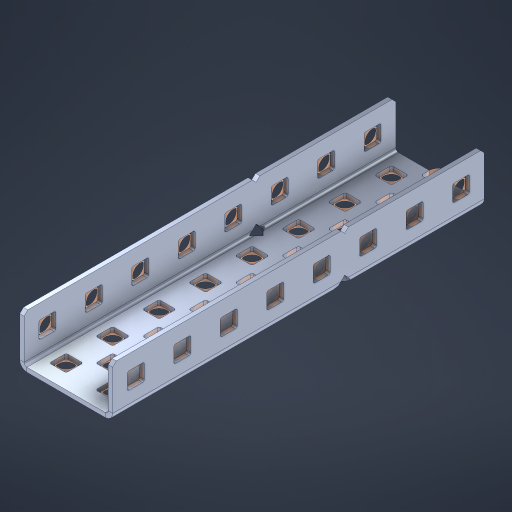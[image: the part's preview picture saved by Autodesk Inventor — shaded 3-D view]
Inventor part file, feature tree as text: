
AUTODESK INVENTOR PART (.ipt)
format: ipt  version: 2023 (Build 270158000, 158)  size: 817,152 bytes
history: native  units: in
note: dims shown in document units (in); Inventor stores cm internally (conversion verified against a paired STEP export)
features: other x47, extrude x38, sheet_metal_op x11, sketch x10, pattern_linear x2, mirror x1, chamfer x1
ambient origin geometry x8: Origin, YZ Plane, XZ Plane, XY Plane, X Axis, Y Axis, Z Axis, Center Point
bodies: Solid1 (feature_tree), Body (feature_tree)
feature tree (110):
  sheet_metal_op  "Flanges"
  other  "Flange Pattern Plane"
  other  "Flange Pattern Sketch"
  sheet_metal_op  "Flange Pattern"
  sheet_metal_op  "Body Pattern"
  pattern_linear  "Center Pattern"  Spacing1=0.0469in  [1 undecoded]
  other  "Arc Length"
  mirror  "Notch Mirror"
  pattern_linear  "Notch Pattern"  Spacing1=0.182in  [1 undecoded]
  chamfer  "End Chamfer"
  extrude  "Half Cut"  Depth=0.02in
  sketch  "Sketch1"  dims[d0=1.0in]
  other  "Plate1"
  sketch  "Sketch2"  dims[d1=4.0in]
  other  "Plate2"
  sheet_metal_op  "Bend1"
  sheet_metal_op  "Corner1"
  sketch  "Sketch3"  dims[d2=0.0469in]
  sketch  "Sketch7"  dims[d3=0.0469in]
  other  "Srf1"
  other  "Srf2"
  sketch  "Sketch8"  dims[d4=0.0234in]
  sketch  "Sketch9"  dims[d5=0.0938in]
  other  "Srf91"
  sheet_metal_op  "Body Pattern Sketch"
  other  "Srf92"
  sketch  "Sketch13"  dims[d6=0.0469in]
  sketch  "Sketch14"  dims[d7=0.5in d8=90.0deg d9=0.0312in]
  sketch  "Sketch15"  dims[d10=0.1875in]
  sketch  "Sketch16"  dims[d11=0.0469in d12=0.0469in d16=0.182in d17=0.02in d18=0.0469in d19=0.0in d20=0.25in d21=0.25in d38=3.1496in d40=0.5in d41=0.7874in d43=1.0in d46=0.172in d47=1.0in d48=0.0in d49=0.182in d50=0.02in d51=0.25in d52=0.25in d53=0.0469in d54=0.0in d55=0.172in d56=1.0in d57=0.0in d58=0.25in d60=3.1496in d62=0.5in d63=0.7874in d65=0.5in d85=0.1227in d86=0.1659in d88=0.04in d89=0.0469in d90=0.0in d91=0.04in d92=0.0491in d95=2.5in d96=0.04in d97=0.25in d98=45.0deg d99=0.25in d100=0.5in d101=0.0in d102=2.497in d106=0.182in d107=0.02in d108=0.5in d109=0.5in d110=0.0469in d111=0.0in d112=0.172in d113=0.5in d114=0.0in d117=0.5in d118=0.5in d119=0.5in]
  other  "Srf786"
  other  "Srf823"
  other  "Srf824"
  other  "Srf825"
  other  "Srf826"
  other  "Srf827"
  other  "Srf828"
  other  "Srf829"
  other  "Srf856"
  other  "Srf857"
  other  "Srf858"
  other  "Srf859"
  other  "Srf860"
  other  "Srf861"
  other  "Srf862"
  other  "Srf889"
  other  "Srf890"
  other  "Srf891"
  other  "Srf892"
  other  "Srf893"
  other  "Srf894"
  other  "Srf895"
  other  "Srf922"
  other  "Srf923"
  other  "Srf924"
  other  "Srf925"
  other  "Srf926"
  other  "Srf959"
  other  "Srf960"
  other  "Srf961"
  other  "Srf962"
  other  "Srf963"
  other  "Srf1143"
  other  "Srf1144"
  other  "Srf1199"
  other  "Srf1200"
  sheet_metal_op  "Flange Stamp"
  sheet_metal_op  "Flange Circle"
  sheet_metal_op  "Body Stamp"
  sheet_metal_op  "Body Circle"
  other  "Center Stamp"
  other  "Center Circle"
  sheet_metal_op  "Notch"
  extrude  "ExtrusionSrf2"  Depth=0.0469in
  extrude  "ExtrusionSrf92"  TaperAngle=0.0deg  [1 undecoded]
  extrude  "ExtrusionSrf823"  Depth=0.5in
  extrude  "ExtrusionSrf824"  Depth=0.5in
  extrude  "ExtrusionSrf825"  Depth=0.5in
  extrude  "ExtrusionSrf826"  Depth=0.5in
  extrude  "ExtrusionSrf827"  Depth=1.0in TaperAngle=0.0deg
  extrude  "ExtrusionSrf828"  Depth=0.5in
  extrude  "ExtrusionSrf829"  Depth=0.02in
  extrude  "ExtrusionSrf856"  Depth=0.5in
  extrude  "ExtrusionSrf857"  Depth=0.5in
  extrude  "ExtrusionSrf858"  Depth=0.0469in
  extrude  "ExtrusionSrf859"  TaperAngle=0.0deg  [1 undecoded]
  extrude  "ExtrusionSrf860"  Depth=0.5in
  extrude  "ExtrusionSrf861"  Depth=1.0in TaperAngle=0.0deg
  extrude  "ExtrusionSrf862"  Depth=0.5in
  extrude  "ExtrusionSrf889"  Depth=0.5in
  extrude  "ExtrusionSrf890"  Depth=0.5in
  extrude  "ExtrusionSrf891"  Depth=0.5in
  extrude  "ExtrusionSrf892"  Depth=0.5in
  extrude  "ExtrusionSrf893"  Depth=0.5in
  extrude  "ExtrusionSrf894"  Depth=0.0469in
  extrude  "ExtrusionSrf895"  TaperAngle=0.0deg  [1 undecoded]
  extrude  "ExtrusionSrf922"  Depth=0.5in
  extrude  "ExtrusionSrf923"  Depth=0.5in
  extrude  "ExtrusionSrf924"  Depth=2.5in
  extrude  "ExtrusionSrf925"  Depth=0.5in TaperAngle=45.0deg
  extrude  "ExtrusionSrf926"  Depth=0.5in
  extrude  "ExtrusionSrf959"  Depth=0.5in TaperAngle=0.0deg
  extrude  "ExtrusionSrf960"  Depth=0.5in
  extrude  "ExtrusionSrf961"  Depth=0.5in
  extrude  "ExtrusionSrf962"  Depth=0.02in
  extrude  "ExtrusionSrf963"  Depth=0.5in
  extrude  "ExtrusionSrf1143"  Depth=0.5in
  extrude  "ExtrusionSrf1144"  Depth=0.0469in
  extrude  "ExtrusionSrf1199"  TaperAngle=0.0deg  [1 undecoded]
  extrude  "ExtrusionSrf1200"  Depth=0.5in
note: 6 required parameter values undecoded (feature->parameter linkage not recoverable at this tier; creation-order binding heuristic only, values carry confidence <= 0.55)
